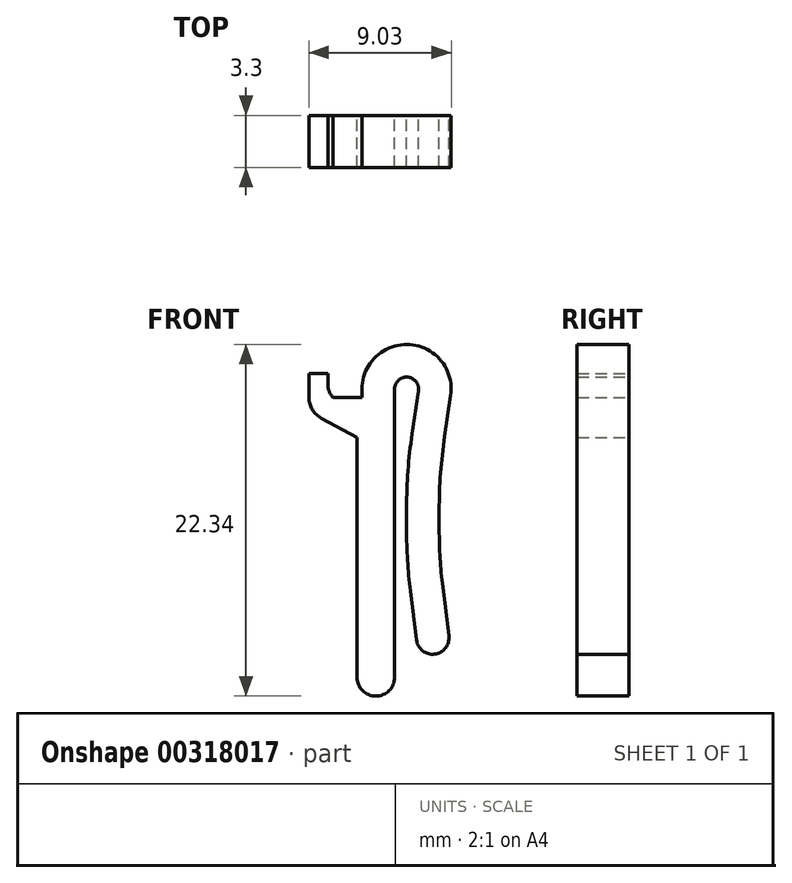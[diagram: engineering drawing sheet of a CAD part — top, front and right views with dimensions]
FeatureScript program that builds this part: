
annotation { "Feature Type Name" : "Feature", "Feature Type Description" : "" }
export const myFeature = defineFeature(function(context is Context, id is Id, definition is map)
    precondition{}
    {
        {
            var Q0;
            Q0=qCreatedBy(makeId("Front.planeOp"),FACE);
            var sketch = newSketch(context, id + "F0", { "sketchPlane" : qUnion([Q0])});
            skLineSegment(sketch, "E0.bottom", {"start": v(-2.72, 18.97) * mm, "end": v(-1.2, 18.97) * mm});
            skLineSegment(sketch, "E1", {"start": v(-2.72, 20.5) * mm, "end": v(-4.24, 20.5) * mm});
            skLineSegment(sketch, "E2", {"start": v(-4.24, 20.5) * mm, "end": v(-4.24, 18.97) * mm});
            skArc(sketch, "E3.trimOffspring", {"start": v(-4.24, 18.97) * mm, "mid": v(-4.03, 18.2) * mm, "end": v(-3.45, 17.64) * mm});
            skLineSegment(sketch, "E4", {"start": v(-1.2, 16.43) * mm, "end": v(-3.45, 17.64) * mm});
            skPoint(sketch, "E5", {"position": v(-1.96, 20.5) * mm});
            skLineSegment(sketch, "E6", {"start": v(-0.88, 18.97) * mm, "end": v(-1.2, 18.97) * mm});
            skLineSegment(sketch, "E7", {"start": v(-3.04, 20.5) * mm, "end": v(-3.04, 19.74) * mm});
            skPoint(sketch, "E7.endSnap0", {"position": v(-4.24, 19.74) * mm});
            skArc(sketch, "E8", {"start": v(-3.04, 19.74) * mm, "mid": v(-2.95, 19.32) * mm, "end": v(-2.72, 18.97) * mm});
            skLineSegment(sketch, "E9", {"start": v(-1.2, 16.43) * mm, "end": v(-1.2, 1.2) * mm});
            skLineSegment(sketch, "E10", {"start": v(1.2, 1.2) * mm, "end": v(1.2, 19.5) * mm});
            skArc(sketch, "E11", {"start": v(2.7, 19.4) * mm, "mid": v(2.01, 20.27) * mm, "end": v(1.2, 19.5) * mm});
            skArc(sketch, "E12", {"start": v(-1.2, 1.2) * mm, "mid": v(0, 0) * mm, "end": v(1.2, 1.2) * mm});
            skArc(sketch, "E13", {"start": v(4.76, 19.1) * mm, "mid": v(2.16, 22.33) * mm, "end": v(-0.88, 19.5) * mm});
            skLineSegment(sketch, "E14", {"start": v(2.3, 16.64) * mm, "end": v(2.7, 19.4) * mm});
            skPoint(sketch, "E15.orphan", {"position": v(2.72, 19.5) * mm});
            skLineSegment(sketch, "E16", {"start": v(1.96, 11.98) * mm, "end": v(1.96, 10.58) * mm});
            skLineSegment(sketch, "E17", {"start": v(2.2, 6.68) * mm, "end": v(2.58, 3.57) * mm});
            skPoint(sketch, "E17.endSnap0", {"position": v(0, 0) * mm});
            skLineSegment(sketch, "E18.0", {"start": v(4.37, 16.49) * mm, "end": v(4.76, 19.1) * mm});
            skLineSegment(sketch, "E18.1", {"start": v(4.03, 11.82) * mm, "end": v(4.03, 10.58) * mm});
            skLineSegment(sketch, "E18.2", {"start": v(4.25, 6.93) * mm, "end": v(4.64, 3.82) * mm});
            skArc(sketch, "E19", {"start": v(2.58, 3.57) * mm, "mid": v(3.74, 2.67) * mm, "end": v(4.64, 3.82) * mm});
            skPoint(sketch, "E20.visualSharp", {"position": v(1.96, 14.32) * mm});
            skArc(sketch, "E20.filletArc", {"start": v(2.3, 16.64) * mm, "mid": v(2.04, 14.32) * mm, "end": v(1.96, 11.98) * mm});
            skPoint(sketch, "E21.visualSharp", {"position": v(1.96, 8.62) * mm});
            skArc(sketch, "E21.filletArc", {"start": v(1.96, 10.58) * mm, "mid": v(2.02, 8.63) * mm, "end": v(2.2, 6.68) * mm});
            skArc(sketch, "E22.0", {"start": v(4.03, 10.58) * mm, "mid": v(4.08, 8.75) * mm, "end": v(4.25, 6.93) * mm});
            skPoint(sketch, "E23.visualSharp", {"position": v(4.03, 14.17) * mm});
            skArc(sketch, "E23.filletArc", {"start": v(4.37, 16.49) * mm, "mid": v(4.11, 14.16) * mm, "end": v(4.03, 11.82) * mm});
            skLineSegment(sketch, "E24", {"start": v(-0.88, 19.5) * mm, "end": v(-0.88, 18.97) * mm});
            skSolve(sketch);
        }
        {
            var Q0;
            Q0 = qSketchRegion(id + "F0", true);
            extrude(context, id + "F1", {"entities" : qUnion([Q0]), "depth" : 3.3 * mm, "offsetDistance" : 25.4 * mm});
        }
    });
